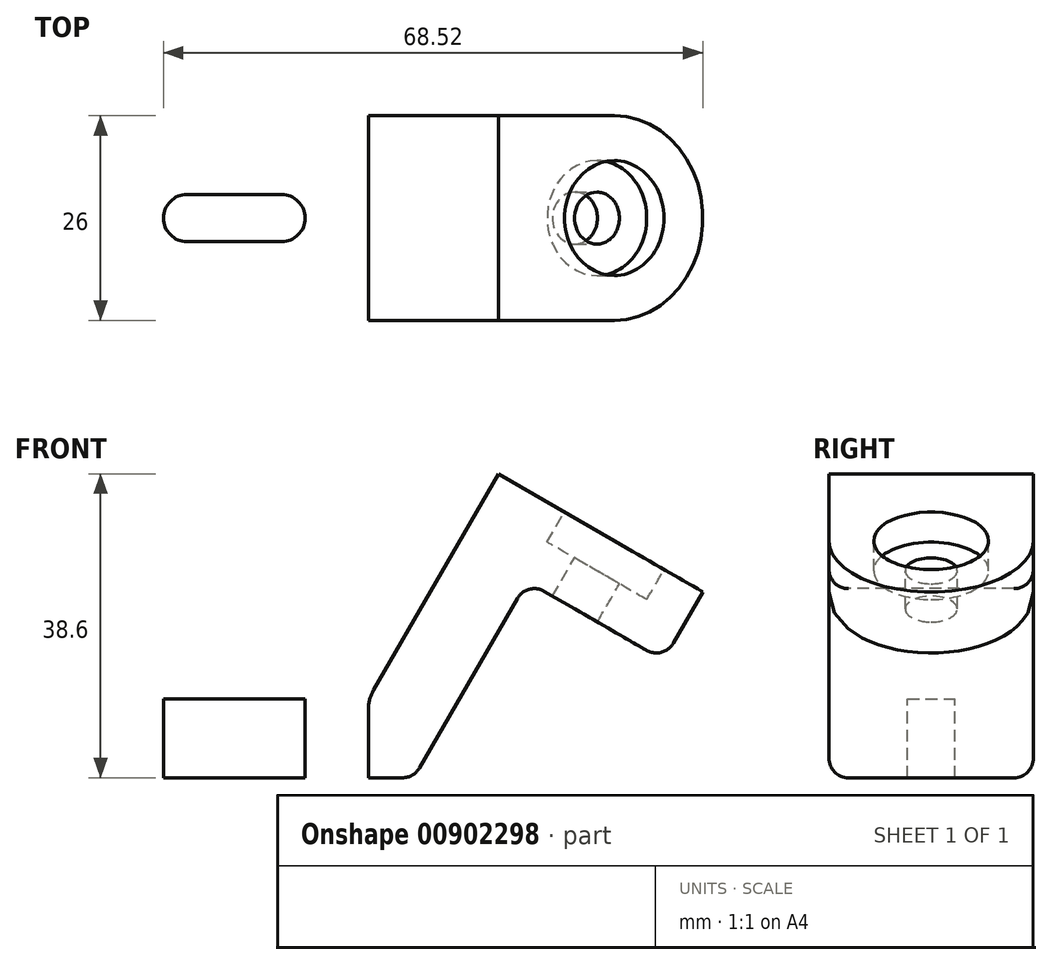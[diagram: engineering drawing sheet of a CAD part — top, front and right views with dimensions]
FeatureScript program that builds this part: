
annotation { "Feature Type Name" : "Feature", "Feature Type Description" : "" }
export const myFeature = defineFeature(function(context is Context, id is Id, definition is map)
    precondition{}
    {
        {
            var Q0;
            Q0=qCreatedBy(makeId("Front.planeOp"),FACE);
            var sketch = newSketch(context, id + "F0", { "sketchPlane" : qUnion([Q0])});
            skLineSegment(sketch, "E0", {"start": v(0, 0) * mm, "end": v(38.8, 0) * mm});
            skLineSegment(sketch, "E1", {"start": v(38.8, 0) * mm, "end": v(53.2, 24.94) * mm});
            skLineSegment(sketch, "E2", {"start": v(53.2, 24.94) * mm, "end": v(70.52, 14.94) * mm});
            skLineSegment(sketch, "E3.0", {"start": v(49.54, 38.6) * mm, "end": v(75.52, 23.6) * mm});
            skLineSegment(sketch, "E3.1", {"start": v(33.03, 10) * mm, "end": v(49.54, 38.6) * mm});
            skLineSegment(sketch, "E3.2", {"start": v(0, 10) * mm, "end": v(33.03, 10) * mm});
            skLineSegment(sketch, "E4", {"start": v(0, 10) * mm, "end": v(0, 0) * mm});
            skLineSegment(sketch, "E5", {"start": v(75.52, 23.6) * mm, "end": v(70.52, 14.94) * mm});
            skSolve(sketch);
        }
        {
            var Q0;
            Q0=makeQuery(id+"F0.imprint","IMPRINT",FACE,{"disambiguationData":[TD([[makeQuery(id+"F0.imprint","IMPRINT",EDGE,{"derivedFrom":sQuery(id+"F0.wireOp",EDGE,"E0")}),1.0]])]});
            extrude(context, id + "F1", {"entities" : qUnion([Q0]), "endBound" : BoundingType.SYMMETRIC, "depth" : 26 * mm, "offsetDistance" : 25 * mm});
        }
        {
            var Q0;
            Q0=makeQuery(id+"F1.opExtrude","SWEPT_FACE",FACE,{"disambiguationData":[OSD([sQuery(id+"F0.wireOp",EDGE,"E3.2")])]});
            var sketch = newSketch(context, id + "F2", { "sketchPlane" : qUnion([Q0])});
            skLineSegment(sketch, "E6", {"start": v(10, 0) * mm, "end": v(22, 0) * mm});
            skArc(sketch, "E7.0.startCap", {"start": v(10, -3) * mm, "mid": v(7, 0) * mm, "end": v(10, 3) * mm});
            skArc(sketch, "E7.0.endCap", {"start": v(22, 3) * mm, "mid": v(25, 0) * mm, "end": v(22, -3) * mm});
            skLineSegment(sketch, "E7.0.left", {"start": v(10, 3) * mm, "end": v(22, 3) * mm});
            skLineSegment(sketch, "E7.0.right", {"start": v(10, -3) * mm, "end": v(22, -3) * mm});
            skSolve(sketch);
        }
        {
            var Q0;
            Q0=makeQuery(id+"F2.imprint","IMPRINT",FACE,{"disambiguationData":[TD([[makeQuery(id+"F2.imprint","IMPRINT",EDGE,{"derivedFrom":sQuery(id+"F2.wireOp",EDGE,"E7.0.startCap")}),-1.0]])]});
            extrude(context, id + "F3", {"entities" : qUnion([Q0]), "operationType" : NewBodyOperationType.REMOVE, "endBound" : BoundingType.THROUGH_ALL, "oppositeDirection" : true, "depth" : 25 * mm, "offsetDistance" : 25 * mm});
        }
        {
            var Q0;
            Q0=makeQuery(id+"F1.opExtrude","SWEPT_EDGE",EDGE,{"disambiguationData":[OSD([sQuery(id+"F0.wireOp",EDGE,"E3.2"),sQuery(id+"F0.wireOp",EDGE,"E4")])]});
            var Q1;
            Q1=makeQuery(id+"F1.opExtrude","SWEPT_EDGE",EDGE,{"disambiguationData":[OSD([sQuery(id+"F0.wireOp",EDGE,"E3.1"),sQuery(id+"F0.wireOp",EDGE,"E3.2")])]});
            fillet(context, id + "F4", {"entities" : qUnion([Q0, Q1]), "radius" : 5 * mm, "tangentPropagation" : true, "allowEdgeOverflow" : false});
        }
        {
            var Q0;
            Q0=makeQuery(id+"F1.opExtrude","SWEPT_EDGE",EDGE,{"disambiguationData":[OSD([sQuery(id+"F0.wireOp",EDGE,"E0"),sQuery(id+"F0.wireOp",EDGE,"E4")])]});
            var Q1;
            Q1=makeQuery(id+"F1.opExtrude","CAP_EDGE",EDGE,{"disambiguationData":[OSD([sQuery(id+"F0.wireOp",EDGE,"E0")])],"isStart":false});
            var Q2;
            Q2=makeQuery(id+"F1.opExtrude","CAP_EDGE",EDGE,{"disambiguationData":[OSD([sQuery(id+"F0.wireOp",EDGE,"E0")])],"isStart":true});
            var Q3;
            Q3=makeQuery(id+"F1.opExtrude","SWEPT_EDGE",EDGE,{"disambiguationData":[OSD([sQuery(id+"F0.wireOp",EDGE,"E0"),sQuery(id+"F0.wireOp",EDGE,"E1")])]});
            var Q4;
            Q4=makeQuery(id+"F1.opExtrude","CAP_EDGE",EDGE,{"disambiguationData":[OSD([sQuery(id+"F0.wireOp",EDGE,"E1")])],"isStart":false});
            var Q5;
            Q5=makeQuery(id+"F1.opExtrude","CAP_EDGE",EDGE,{"disambiguationData":[OSD([sQuery(id+"F0.wireOp",EDGE,"E1")])],"isStart":true});
            var Q6;
            Q6=makeQuery(id+"F1.opExtrude","SWEPT_EDGE",EDGE,{"disambiguationData":[OSD([sQuery(id+"F0.wireOp",EDGE,"E1"),sQuery(id+"F0.wireOp",EDGE,"E2")])]});
            var Q7;
            Q7=makeQuery(id+"F1.opExtrude","CAP_EDGE",EDGE,{"disambiguationData":[OSD([sQuery(id+"F0.wireOp",EDGE,"E2")])],"isStart":false});
            var Q8;
            Q8=makeQuery(id+"F1.opExtrude","CAP_EDGE",EDGE,{"disambiguationData":[OSD([sQuery(id+"F0.wireOp",EDGE,"E2")])],"isStart":true});
            var Q9;
            Q9=makeQuery(id+"F1.opExtrude","SWEPT_EDGE",EDGE,{"disambiguationData":[OSD([sQuery(id+"F0.wireOp",EDGE,"E2"),sQuery(id+"F0.wireOp",EDGE,"E5")])]});
            fillet(context, id + "F5", {"entities" : qUnion([Q0, Q1, Q2, Q3, Q4, Q5, Q6, Q7, Q8, Q9]), "radius" : 2.5 * mm, "tangentPropagation" : true, "allowEdgeOverflow" : false});
        }
        {
            var Q0;
            Q0=makeQuery(id+"F1.opExtrude","CAP_EDGE",EDGE,{"disambiguationData":[OSD([sQuery(id+"F0.wireOp",EDGE,"E5")])],"isStart":false});
            var Q1;
            Q1=makeQuery(id+"F1.opExtrude","CAP_EDGE",EDGE,{"disambiguationData":[OSD([sQuery(id+"F0.wireOp",EDGE,"E5")])],"isStart":true});
            fillet(context, id + "F6", {"entities" : qUnion([Q0, Q1]), "radius" : 13 * mm, "tangentPropagation" : true, "allowEdgeOverflow" : false});
        }
        {
            var Q0;
            Q0=makeQuery(id+"F1.opExtrude","SWEPT_FACE",FACE,{"disambiguationData":[OSD([sQuery(id+"F0.wireOp",EDGE,"E3.0")])]});
            var sketch = newSketch(context, id + "F7", { "sketchPlane" : qUnion([Q0])});
            skCircle(sketch, "E8", {"center": v(40.6, 0) * mm, "radius": 3.3 * mm});
            skCircle(sketch, "E9", {"center": v(40.6, 0) * mm, "radius": 7.3 * mm});
            skSolve(sketch);
        }
        {
            var Q0;
            Q0=makeQuery(id+"F7.imprint","IMPRINT",FACE,{"disambiguationData":[TD([[makeQuery(id+"F7.imprint","IMPRINT",EDGE,{"derivedFrom":sQuery(id+"F7.wireOp",EDGE,"E8")}),1.0]])]});
            extrude(context, id + "F8", {"entities" : qUnion([Q0]), "operationType" : NewBodyOperationType.REMOVE, "endBound" : BoundingType.THROUGH_ALL, "oppositeDirection" : true, "depth" : 25 * mm, "offsetDistance" : 25 * mm});
        }
        {
            var Q0;
            Q0=makeQuery(id+"F1.opExtrude","SWEPT_FACE",FACE,{"disambiguationData":[OSD([sQuery(id+"F0.wireOp",EDGE,"E3.0")])]});
            var sketch = newSketch(context, id + "F9", { "sketchPlane" : qUnion([Q0])});
            skSolve(sketch);
        }
        {
            var Q0;
            Q0 = qSketchRegion(id + "F9", true);
            var Q1;
            Q1 = qSketchRegion(id + "F7", true);
            extrude(context, id + "F10", {"entities" : qUnion([Q0, Q1]), "operationType" : NewBodyOperationType.REMOVE, "oppositeDirection" : true, "depth" : 4.4 * mm, "offsetDistance" : 25 * mm});
        }
    });
